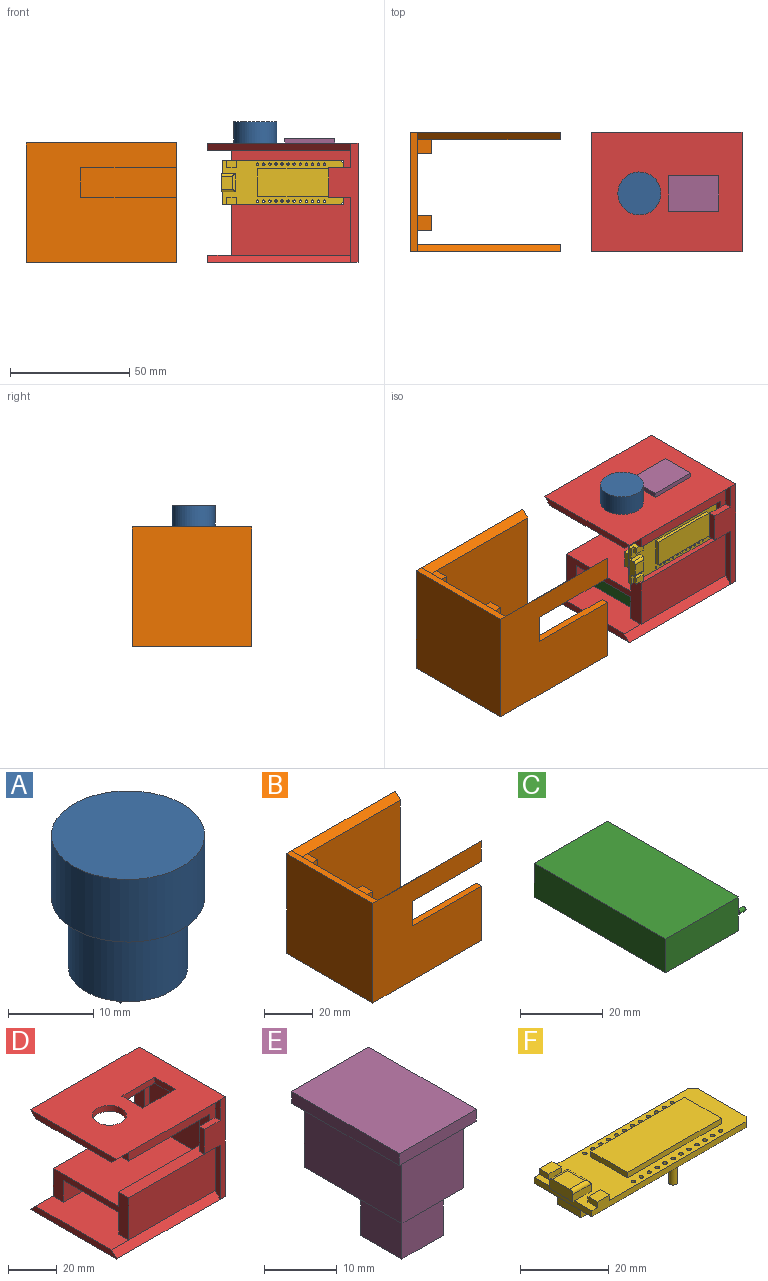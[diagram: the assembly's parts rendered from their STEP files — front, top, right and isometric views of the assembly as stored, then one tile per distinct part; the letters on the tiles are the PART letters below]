
ASSEMBLY  parts=6 mates=5
PART A: 15 faces, bbox 18x18x22 mm
  f0: cylinder r=9mm len=18mm, axis (0,0,-1), area 508.9mm2, adj f1,f2
  f1: plane 18x18mm, normal (0,0,1), area 254.5mm2, adj f0
  f2: plane 18x18mm, normal (0,0,-1), area 100.5mm2, adj f0,f3
  f3: cylinder r=7mm len=14mm, axis (0,0,1), area 439.8mm2, adj f2,f4
  f4: plane 14x14mm, normal (0,0,-1), area 150.9mm2, adj f3,f5,f6,f7,f8,f10,f11,f12
  f5: plane 3x0.5mm, normal (0,1,0), area 1.5mm2, adj f4,f6,f8,f9
  f6: plane 3x3mm, normal (1,0,0), area 9mm2, adj f4,f5,f7,f9
  f7: plane 3x0.5mm, normal (0,-1,0), area 1.5mm2, adj f4,f6,f8,f9
  f8: plane 3x3mm, normal (-1,0,0), area 9mm2, adj f4,f5,f7,f9
  f9: plane 3x0.5mm, normal (0,0,-1), area 1.5mm2, adj f5,f6,f7,f8
  f10: plane 3x0.5mm, normal (0,1,0), area 1.5mm2, adj f4,f11,f13,f14
  f11: plane 3x3mm, normal (1,0,0), area 9mm2, adj f4,f10,f12,f14
  f12: plane 3x0.5mm, normal (0,-1,0), area 1.5mm2, adj f4,f11,f13,f14
  f13: plane 3x3mm, normal (-1,0,0), area 9mm2, adj f4,f10,f12,f14
  f14: plane 3x0.5mm, normal (0,0,-1), area 1.5mm2, adj f10,f11,f12,f13
PART B: 27 faces, bbox 63x50x50 mm
  f0: plane 60x44mm, normal (0,1,0), area 2144.1mm2, adj f1,f2,f12,f13,f14,f15,f16,f17
  f1: plane 10.37x3mm, normal (1,0,0), area 26.6mm2, adj f0,f3,f13,f15
  f2: plane 50x50mm, normal (1,0,0), area 1690mm2, adj f0,f4,f5,f8,f10,f12,f13,f18
  f3: plane 63x50mm, normal (0,-1,0), area 2654.1mm2, adj f1,f4,f5,f7,f12,f13,f14,f15
  f4: plane 50x3mm, normal (0,0,1), area 150mm2, adj f2,f3,f6,f7
  f5: plane 50x3mm, normal (0,0,-1), area 150mm2, adj f2,f3,f6,f7
  f6: plane 63x50mm, normal (0,1,0), area 3150mm2, adj f4,f5,f7,f8,f10,f11
  f7: plane 50x50mm, normal (-1,0,0), area 2500mm2, adj f3,f4,f5,f6
  f8: plane 60x3mm, normal (0,-0.71,0.71), area 254.6mm2, adj f2,f6,f9,f11,f18
  f9: plane 54x44mm, normal (0,-1,0), area 2376mm2, adj f8,f10,f11,f21
  f10: plane 60x3mm, normal (0,-0.71,-0.71), area 254.6mm2, adj f2,f6,f9,f11,f20
  f11: plane 50x3mm, normal (1,0,0), area 141mm2, adj f6,f8,f9,f10
  f12: plane 60x3mm, normal (0,0.71,-0.71), area 254.6mm2, adj f0,f2,f3,f14
  f13: plane 60x3mm, normal (0,0.71,0.71), area 254.6mm2, adj f0,f1,f2,f3
  f14: plane 27.24x3mm, normal (1,0,0), area 77.2mm2, adj f0,f3,f12,f17
  f15: plane 40.04x3mm, normal (0,0,-1), area 120.1mm2, adj f0,f1,f3,f16
  f16: plane 12.39x3mm, normal (1,0,0), area 37.2mm2, adj f0,f3,f15,f17
  f17: plane 40.04x3mm, normal (0,0,1), area 120.1mm2, adj f0,f3,f14,f16
  f18: plane 6x6mm, normal (0,0,1), area 36mm2, adj f2,f8,f19,f21
  f19: plane 44x6mm, normal (0,-1,0), area 264mm2, adj f2,f18,f20,f21
  f20: plane 6x6mm, normal (0,0,-1), area 36mm2, adj f2,f10,f19,f21
  f21: plane 44x6mm, normal (1,0,0), area 264mm2, adj f9,f18,f19,f20
  f22: plane 6x6mm, normal (0,0,1), area 36mm2, adj f2,f23,f25,f26
  f23: plane 44x6mm, normal (0,-1,0), area 264mm2, adj f2,f22,f24,f26
  f24: plane 6x6mm, normal (0,0,-1), area 36mm2, adj f2,f23,f25,f26
  f25: plane 44x6mm, normal (0,1,0), area 264mm2, adj f2,f22,f24,f26
  f26: plane 44x6mm, normal (1,0,0), area 264mm2, adj f22,f23,f24,f25
PART C: 9 faces, bbox 27x45.6x10 mm
  f0: plane 45x10mm, normal (-1,0,0), area 450mm2, adj f1,f3,f4,f5
  f1: plane 25x10mm, normal (0,-1,0), area 250mm2, adj f0,f2,f4,f5,f6
  f2: plane 45x10mm, normal (1,0,0), area 449.4mm2, adj f1,f3,f4,f5,f8
  f3: plane 25x10mm, normal (0,1,0), area 250mm2, adj f0,f2,f4,f5
  f4: plane 45x25mm, normal (0,0,1), area 1125mm2, adj f0,f1,f2,f3
  f5: plane 45x25mm, normal (0,0,-1), area 1125mm2, adj f0,f1,f2,f3
  f6: plane 1.2x0.6mm, normal (-1,0,0), area 0.6mm2, adj f1,f8
  f7: plane 1.2x1.2mm, normal (1,0,0), area 1.1mm2, adj f8
  f8: cylinder r=0.6mm len=2mm, axis (1,0,0), area 7.5mm2, adj f2,f6,f7
PART D: 42 faces, bbox 63x50x50 mm
  f0: plane 10.37x3mm, normal (-1,0,0), area 26.6mm2, adj f1,f17,f20,f40
  f1: plane 50x7.37mm, normal (0,-1,0), area 226.4mm2, adj f0,f5,f17,f35,f36,f40
  f2: plane 60x44mm, normal (0,0,1), area 2040mm2, adj f9,f12,f13,f15,f29,f30,f31
  f3: plane 50x32mm, normal (0,0,-1), area 1600mm2, adj f9,f29,f30,f31
  f4: plane 50x38mm, normal (0,0,1), area 1882mm2, adj f7,f27,f29,f32,f33,f34
  f5: plane 18.5x6mm, normal (-1,0,0), area 111mm2, adj f1,f28,f34,f35,f37,f38
  f6: plane 60x44mm, normal (0,0,-1), area 1940.1mm2, adj f7,f16,f17,f18,f22,f23,f24,f25
  f7: plane 32x30mm, normal (-1,0,0), area 960mm2, adj f4,f6,f32,f34
  f8: plane 27.24x3mm, normal (-1,0,0), area 77.2mm2, adj f13,f20,f28,f39
  f9: plane 32x11mm, normal (-1,0,0), area 352mm2, adj f2,f3,f30,f31
  f10: plane 50x3mm, normal (-1,0,0), area 141mm2, adj f12,f16,f19,f27
  f11: plane 63x50mm, normal (0,0,1), area 2768.1mm2, adj f16,f17,f18,f19,f20,f21,f22,f23
  f12: plane 60x3mm, normal (0,0.71,0.71), area 254.6mm2, adj f2,f10,f14,f15,f27
  f13: plane 60x3mm, normal (0,-0.71,0.71), area 254.6mm2, adj f2,f8,f14,f15,f28
  f14: plane 63x50mm, normal (0,0,-1), area 3150mm2, adj f12,f13,f15,f19,f20,f21
  f15: plane 50x3mm, normal (-1,0,0), area 141mm2, adj f2,f12,f13,f14
  f16: plane 60x3mm, normal (0,0.71,-0.71), area 254.6mm2, adj f6,f10,f11,f18,f27
  f17: plane 60x3mm, normal (0,-0.71,-0.71), area 254.6mm2, adj f0,f1,f6,f11,f18
  f18: plane 50x3mm, normal (-1,0,0), area 141mm2, adj f6,f11,f16,f17
  f19: plane 50x3mm, normal (0,1,0), area 150mm2, adj f10,f11,f14,f21
  f20: plane 50x12.21mm, normal (0,-1,0), area 264.1mm2, adj f0,f8,f11,f14,f21,f39,f40,f41
  f21: plane 50x50mm, normal (1,0,0), area 2500mm2, adj f11,f14,f19,f20
  f22: plane 12x3mm, normal (1,0,0), area 36mm2, adj f6,f11,f23,f25
  f23: plane 19x3mm, normal (0,1,0), area 57mm2, adj f6,f11,f22,f24
  f24: plane 12x3mm, normal (-1,0,0), area 36mm2, adj f6,f11,f23,f25
  f25: plane 19x3mm, normal (0,-1,0), area 57mm2, adj f6,f11,f22,f24
  f26: cylinder r=7mm len=14mm, axis (0,0,1), area 131.9mm2, adj f6,f11
  f27: plane 50x44mm, normal (0,1,0), area 790mm2, adj f4,f10,f12,f16,f29,f33
  f28: plane 50x24.24mm, normal (0,-1,0), area 1067mm2, adj f5,f8,f13,f29,f37,f39
  f29: plane 44x21.15mm, normal (-1,0,0), area 306.9mm2, adj f2,f3,f4,f27,f28,f30,f31,f34
  f30: plane 50x11mm, normal (0,-1,0), area 550mm2, adj f2,f3,f9,f29
  f31: plane 50x11mm, normal (0,1,0), area 550mm2, adj f2,f3,f9,f29
  f32: plane 30x3mm, normal (0,-1,0), area 90mm2, adj f4,f6,f7,f33
  f33: plane 30x6mm, normal (-1,0,0), area 180mm2, adj f4,f6,f27,f32
  f34: plane 50x30mm, normal (0,1,0), area 630.5mm2, adj f4,f5,f6,f7,f29,f35,f36,f37
  f35: plane 47x6mm, normal (0,0,-1), area 282mm2, adj f1,f5,f34,f36
  f36: plane 6x4.35mm, normal (-1,0,0), area 26.1mm2, adj f1,f6,f34,f35
  f37: plane 47x6mm, normal (0,0,1), area 282mm2, adj f5,f28,f29,f34
  f38: plane 12.39x6.21mm, normal (0,1,0), area 76.9mm2, adj f5,f39,f40,f41
  f39: plane 9.21x3mm, normal (0,0,-1), area 27.6mm2, adj f8,f20,f28,f38,f41
  f40: plane 9.21x3mm, normal (0,0,1), area 27.6mm2, adj f0,f1,f20,f38,f41
  f41: plane 12.39x3mm, normal (-1,0,0), area 37.2mm2, adj f20,f38,f39,f40
PART E: 16 faces, bbox 15x21x21 mm
  f0: plane 19x11mm, normal (-1,0,0), area 209mm2, adj f1,f3,f4,f10
  f1: plane 12x11mm, normal (0,-1,0), area 132mm2, adj f0,f2,f4,f10
  f2: plane 19x11mm, normal (1,0,0), area 209mm2, adj f1,f3,f4,f10
  f3: plane 12x11mm, normal (0,1,0), area 132mm2, adj f0,f2,f4,f10
  f4: plane 19x12mm, normal (0,0,-1), area 164mm2, adj f0,f1,f2,f3,f11,f12,f13,f14
  f5: plane 15x2mm, normal (0,-1,0), area 30mm2, adj f6,f8,f9,f10
  f6: plane 21x2mm, normal (1,0,0), area 42mm2, adj f5,f7,f9,f10
  f7: plane 15x2mm, normal (0,1,0), area 30mm2, adj f6,f8,f9,f10
  f8: plane 21x2mm, normal (-1,0,0), area 42mm2, adj f5,f7,f9,f10
  f9: plane 21x15mm, normal (0,0,1), area 315mm2, adj f5,f6,f7,f8
  f10: plane 21x15mm, normal (0,0,-1), area 87mm2, adj f0,f1,f2,f3,f5,f6,f7,f8
  f11: plane 8x8mm, normal (1,0,0), area 64mm2, adj f4,f12,f14,f15
  f12: plane 8x8mm, normal (0,-1,0), area 64mm2, adj f4,f11,f13,f15
  f13: plane 8x8mm, normal (-1,0,0), area 64mm2, adj f4,f12,f14,f15
  f14: plane 8x8mm, normal (0,1,0), area 64mm2, adj f4,f11,f13,f15
  f15: plane 8x8mm, normal (0,0,-1), area 64mm2, adj f11,f12,f13,f14
PART F: 68 faces, bbox 51.4x18.5x9.7 mm
  f0: plane 50.75x18.5mm, normal (0,0,1), area 505mm2, adj f2,f3,f4,f5,f6,f7,f8,f9
  f1: plane 50.75x18.5mm, normal (0,0,-1), area 873.2mm2, adj f2,f3,f4,f5,f6,f7,f31,f32
  f2: plane 49.25x3.15mm, normal (0,1,0), area 87.3mm2, adj f0,f1,f3,f7,f22,f24,f25
  f3: plane 18.5x1.65mm, normal (-1,0,0), area 30.5mm2, adj f0,f1,f2,f4,f13
  f4: plane 49.25x3.15mm, normal (0,-1,0), area 87.3mm2, adj f0,f1,f3,f5,f26,f28,f29
  f5: plane 1.65x1.5mm, normal (0.71,-0.71,0), area 3.5mm2, adj f0,f1,f4,f6
  f6: plane 15.5x1.65mm, normal (1,0,0), area 25.6mm2, adj f0,f1,f5,f7
  f7: plane 1.65x1.5mm, normal (0.71,0.71,0), area 3.5mm2, adj f0,f1,f2,f6
  f8: plane 11.65x1.5mm, normal (1,0,0), area 17.5mm2, adj f0,f9,f11,f12
  f9: plane 30x1.5mm, normal (0,1,0), area 45mm2, adj f0,f8,f10,f12
  f10: plane 11.65x1.5mm, normal (-1,0,0), area 17.5mm2, adj f0,f9,f11,f12
  f11: plane 30x1.5mm, normal (0,-1,0), area 45mm2, adj f0,f8,f10,f12
  f12: plane 30x11.65mm, normal (0,0,1), area 349.5mm2, adj f8,f9,f10,f11
  f13: plane 7.5x0.6mm, normal (0,0,-1), area 4.5mm2, adj f3,f14,f16,f17
  f14: plane 5.84x2mm, normal (0,-1,0), area 11.7mm2, adj f0,f13,f15,f17,f21
  f15: plane 7.5x2mm, normal (1,0,0), area 15mm2, adj f0,f14,f16,f20
  f16: plane 5.84x2mm, normal (0,1,0), area 11.7mm2, adj f0,f13,f15,f17,f19
  f17: plane 7.5x3mm, normal (-1,0,0), area 22.1mm2, adj f13,f14,f16,f18,f19,f21
  f18: plane 5.5x4.84mm, normal (0,0,1), area 26.6mm2, adj f17,f19,f20,f21
  f19: cylinder r=1mm len=5.84mm, axis (1,0,0), area 8.6mm2, adj f16,f17,f18,f20
  f20: cylinder r=1mm len=7.5mm, axis (0,-1,0), area 10.6mm2, adj f15,f18,f19,f21
  f21: cylinder r=1mm len=5.84mm, axis (-1,0,0), area 8.6mm2, adj f14,f17,f18,f20
  f22: plane 3x1.5mm, normal (-1,0,0), area 4.5mm2, adj f0,f2,f23,f25
  f23: plane 4x1.5mm, normal (0,-1,0), area 6mm2, adj f0,f22,f24,f25
  f24: plane 3x1.5mm, normal (1,0,0), area 4.5mm2, adj f0,f2,f23,f25
  f25: plane 4x3mm, normal (0,0,1), area 12mm2, adj f2,f22,f23,f24
  f26: plane 3x1.5mm, normal (1,0,0), area 4.5mm2, adj f0,f4,f27,f29
  f27: plane 4x1.5mm, normal (0,1,0), area 6mm2, adj f0,f26,f28,f29
  f28: plane 3x1.5mm, normal (-1,0,0), area 4.5mm2, adj f0,f4,f27,f29
  f29: plane 4x3mm, normal (0,0,1), area 12mm2, adj f4,f26,f27,f28
  f30: cylinder r=0.5mm len=1.65mm, axis (0,0,1), area 5.2mm2, adj f0,f65
  f31: cylinder r=0.5mm len=1.65mm, axis (0,0,1), area 5.2mm2, adj f0,f1
  f32: cylinder r=0.5mm len=1.65mm, axis (0,0,1), area 5.2mm2, adj f0,f1
  f33: cylinder r=0.5mm len=1.65mm, axis (0,0,1), area 5.2mm2, adj f0,f1
  f34: cylinder r=0.5mm len=1.65mm, axis (0,0,1), area 5.2mm2, adj f0,f1
  f35: cylinder r=0.5mm len=1.65mm, axis (0,0,1), area 5.2mm2, adj f0,f1
  f36: cylinder r=0.5mm len=1.65mm, axis (0,0,1), area 5.2mm2, adj f0,f1
  f37: cylinder r=0.5mm len=1.65mm, axis (0,0,1), area 5.2mm2, adj f0,f59
  f38: cylinder r=0.5mm len=1.65mm, axis (0,0,1), area 5.2mm2, adj f0,f1
  f39: cylinder r=0.5mm len=1.65mm, axis (0,0,1), area 5.2mm2, adj f0,f62
  f40: cylinder r=0.5mm len=1.65mm, axis (0,0,1), area 5.2mm2, adj f0,f1
  f41: cylinder r=0.5mm len=1.65mm, axis (0,0,1), area 5.2mm2, adj f0,f1
  f42: cylinder r=0.5mm len=1.65mm, axis (0,0,1), area 5.2mm2, adj f0,f1
  f43: cylinder r=0.5mm len=1.65mm, axis (0,0,1), area 5.2mm2, adj f0,f1
  f44: cylinder r=0.5mm len=1.65mm, axis (0,0,1), area 5.2mm2, adj f0,f1
  f45: cylinder r=0.5mm len=1.65mm, axis (0,0,1), area 5.2mm2, adj f0,f1
  f46: cylinder r=0.5mm len=1.65mm, axis (0,0,1), area 5.2mm2, adj f0,f1
  f47: cylinder r=0.5mm len=1.65mm, axis (0,0,1), area 5.2mm2, adj f0,f1
  f48: cylinder r=0.5mm len=1.65mm, axis (0,0,1), area 5.2mm2, adj f0,f1
  f49: cylinder r=0.5mm len=1.65mm, axis (0,0,1), area 5.2mm2, adj f0,f1
  f50: cylinder r=0.5mm len=1.65mm, axis (0,0,1), area 5.2mm2, adj f0,f1
  f51: cylinder r=0.5mm len=1.65mm, axis (0,0,1), area 5.2mm2, adj f0,f1
  f52: cylinder r=0.5mm len=1.65mm, axis (0,0,1), area 5.2mm2, adj f0,f1
  f53: cylinder r=0.5mm len=1.65mm, axis (0,0,1), area 5.2mm2, adj f0,f1
  f54: plane 7.5x4mm, normal (-1,0,0), area 30mm2, adj f1,f55,f57,f58
  f55: plane 5x4mm, normal (0,1,0), area 20mm2, adj f1,f54,f56,f58
  f56: plane 7.5x4mm, normal (1,0,0), area 30mm2, adj f1,f55,f57,f58
  f57: plane 5x4mm, normal (0,-1,0), area 20mm2, adj f1,f54,f56,f58
  f58: plane 7.5x5mm, normal (0,0,-1), area 37.5mm2, adj f54,f55,f56,f57
  f59: plane 1x1mm, normal (0,0,1), area 0.8mm2, adj f37
  f60: cylinder r=1mm len=5mm, axis (0,0,1), area 31.4mm2, adj f1,f61
  f61: plane 2x2mm, normal (0,0,-1), area 3.1mm2, adj f60
  f62: plane 1x1mm, normal (0,0,1), area 0.8mm2, adj f39
  f63: cylinder r=1mm len=5mm, axis (0,0,1), area 31.4mm2, adj f1,f64
  f64: plane 2x2mm, normal (0,0,-1), area 3.1mm2, adj f63
  f65: plane 1x1mm, normal (0,0,1), area 0.8mm2, adj f30
  f66: cylinder r=1mm len=5mm, axis (0,0,1), area 31.4mm2, adj f1,f67
  f67: plane 2x2mm, normal (0,0,-1), area 3.1mm2, adj f66
PLACE A t=(-21.51,5.98,13.35)mm
PLACE B t=(-117.6,0.03,-11.76)mm
PLACE C rot(axis=(-0.71,-0.71,0),180deg) t=(-26.5,-5.83,-23.15)mm
PLACE D t=(-44.5,0.09,-11.79)mm
PLACE E rot(axis=(0,0,-1),90deg) t=(-8.21,11.98,2.35)mm
PLACE F rot(axis=(1,0,0),90deg) t=(-35.25,-11.51,6)mm
MATE fastened D.f9 <-> C.f3  axis (-1,0,0) through (18.5,6.67,-28.15)mm
MATE fastened D.f5 <-> F.f6  axis (-1,0,0) through (15.5,-12.33,-3.25)mm
MATE slider D.f18 <-> B.f2  axis (-1,0,0) through (-41.5,6.67,11.88)mm
MATE fastened E.f10 <-> D.f11  axis (0,0,-1) through (1.29,5.98,13.35)mm
MATE fastened A.f0 <-> D.f26  axis (0,0,-1) through (-21.51,5.98,13.35)mm
